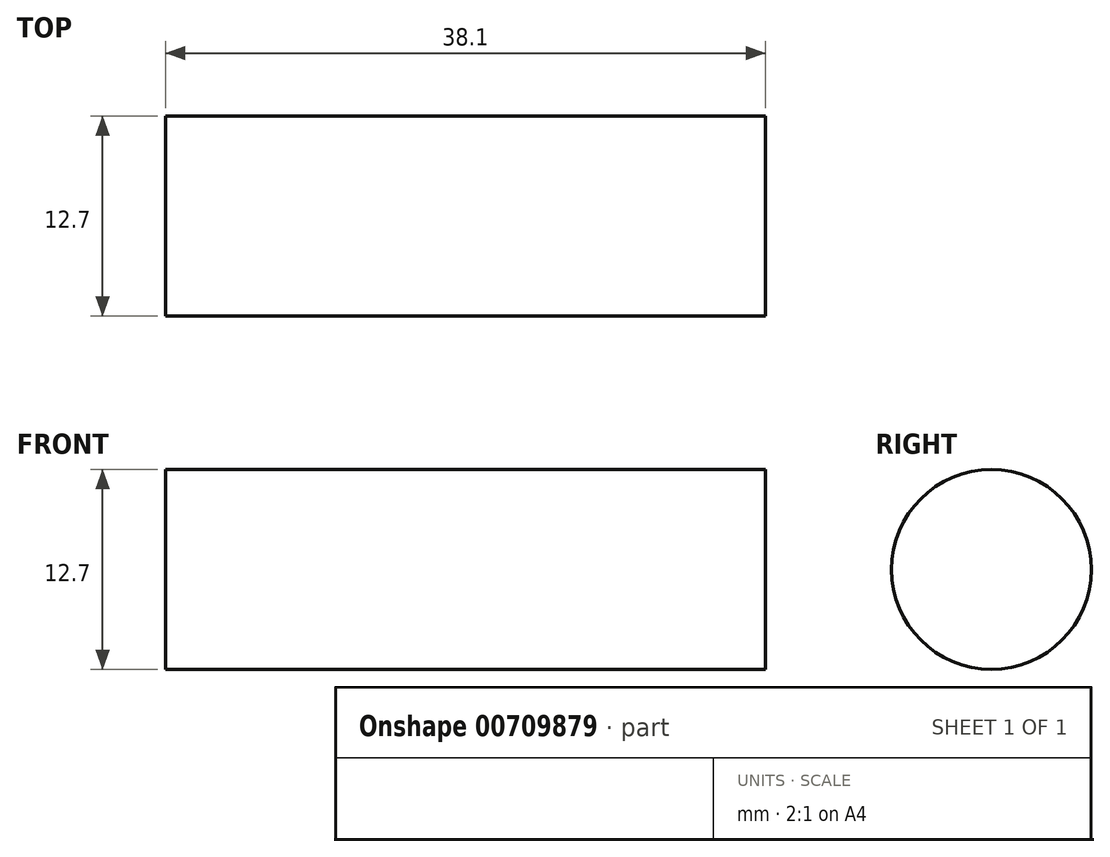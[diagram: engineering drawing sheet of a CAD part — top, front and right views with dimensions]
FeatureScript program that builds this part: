
annotation { "Feature Type Name" : "Feature", "Feature Type Description" : "" }
export const myFeature = defineFeature(function(context is Context, id is Id, definition is map)
    precondition{}
    {
        {
            var Q0;
            Q0=qCreatedBy(makeId("Right.planeOp"),FACE);
            var sketch = newSketch(context, id + "F0", { "sketchPlane" : qUnion([Q0])});
            skCircle(sketch, "E0", {"center": v(0, 0) * mm, "radius": 6.35 * mm});
            skSolve(sketch);
        }
        {
            var Q0;
            Q0=qSketchRegion(id+"F0",true);
            extrude(context, id + "F1", {"entities" : qUnion([Q0]), "endBound" : BoundingType.SYMMETRIC, "depth" : 38.1 * mm, "offsetDistance" : 25.4 * mm});
        }
    });
